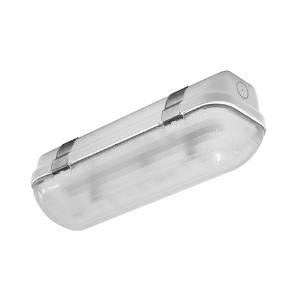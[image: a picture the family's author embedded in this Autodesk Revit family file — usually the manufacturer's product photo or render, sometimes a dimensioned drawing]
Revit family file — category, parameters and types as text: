
# Revit family: 3f_filippi_-_3f_linda_compatta_3f_filippi_-_5066_-_3f_linda_led_1x6w_l300
name_source: partatom
category: Lighting Fixtures
units: mm (PartAtom-declared; Revit-internal decimal feet)

## family parameters
Cut with Voids When Loaded = No
Host = Face
Light Source = No
Part Type = Normal
Room Calculation Point = No
Round Connector Dimension = Use Diameter
Shared = No

## types (1)
- 3F Filippi - 3F Linda Compatta (1 x LED, 883 lm, 7.5 W, 4000 K)
    Apparent Load = 8 VA
    Approval mark = ENEC
    CIE Flux Codes = 44 76 94 97 100
    Color Rendering = 80
    Color Temperature = 4000 K
    Control Gear = Electronic ballast
    Default Elevation = 1800 mm
    Description = ILLUMINOTECHNICAL
Luminous efficiency 100% (DLOR 97%, ULOR 3%).
Initial luminous flux of the luminaire 883 lm.
Controlled symmetric distribution.
Installation Interdistance Transv.D = 1.82 x hu - Long.D = 1.20 x hu.
Tabular UGR (CIE 117 - 4H-8H; S=0.25H; 70/50/20): RUG 21.6 - 22.5.
Beam angle: 110° - 66°.
Luminous efficacy 118 lm/W.
Lifetime (L93/B10): 30000 h. (tq+25°C)
Lifetime (L90/B10): 50000 h. (tq+25°C)
Lifetime (L85/B10): 80000 h. (tq+25°C)
Lifetime (L80/B10): 100000 h. (tq+25°C)
Sudden decreased luminous flux after 50000 hours: 0% (C0).
Photobiological safety in compliance with IEC/TR 62778: RG0 risk exempt, (IEC 62471).
In compliance with IEC/EN 62722-2-1 - IEC/EN 62717 standards.

SOURCE
Linear LED module 6W/840.
Energy efficiency class (UE 2019/2020 - UE 2019/2015): D.
CIE 13.3 Colour rendering index: CRI >80 (R9 <50%).
IES TM-30 Fidelity Index: Rf = 84 Rg = 95.
CCT nominal colour temperature 4000 K.
Colour initial tolerance (MacAdam): SDCM 3.

MECHANICAL
Self-extinguishing V2 polycarbonate housing, injection moulded, RAL 7035 grey.
Ecologic anti-aging injected sealing gasket.
Gear-holder reflector in hot-dip galvanised steel, painted with white polyester base.
Diffuser in self-extinguishing V2 polycarbonate, photo-engraved interior, UV stabilised, injection moulded with smooth outer surface.
Snug fit safety snap-lock clips for diffuser mounting in stainless steel, screwdriver opening.
Luminaire with limited surface temperature. - D - (EN 60598-2-24)
Dimensions: 300x100 mm, height 100 mm. Weight 0.555 kg.
IP66 protection degree.
Mechanical strength to impacts IK10 (20 joule).
Glow-wire test resistance 850°C.

ELECTRICAL
Halogen Free electronic wiring 230V-50/60Hz, power factor 0.88, THD <25%, constant output current, SELV, class I, 1 driver.
Power of the luminaire 7.5 W.
CE - IEC 60598-1 - EN 60598-1.
Flicker: <15%.
Luminaire compliant with EN 60598-2-22 for power supply from a centralised emergency system CPSS (Central Power Supply System), not incorporated in the luminaire - high risk areas excluded. The default power and flux are 100% in AC and 100% in DC.
Ambient temperature from -20°C to +35°C.
Temperature class T6 max 85°C.
Relative humidity UR: <85%.

INSTALLATION
Ceiling / Wall.
All accessories dedicated to this product are available on the Catalog and on our website www.3F-Filippi.com.

APPLICATIONS
Suitable product for food production plants (HACCP), IFS (Food Version 6), BRC (GSFS Food Version 7).
Dry, dusty indoor environments, subject to occasional water splashes.
Virtually shatterproof polycarbonate compatibly with the fumes / atmospheres that compromise the elasticity of plastic materials.
Not suitable for installation on surfaces subject to important vibrations, exposed to weather conditions, on ropes or poles.
Suitable for illumination of public car parks and parking grounds referred to DIN 67528:2018-04.

WARNING
Fixture not suitable for cold stores with an ambient temperature <0°C and/or relative humidity >85%.
Luminaire designed for disposal/recycling at end-of-life.
Replaceable (LED only) light source by a professional. Replaceable control gear by a professional.
    Height = 100 mm  [stored 0.328084 ft]
    Lamp = 1 x LED
    Lamp Light Flux = 883 lm
    Lamp Power = 7.5 W
    Lamp count = 1
    Length = 300 mm
    Lifetime = 50000 h
    Luminous efficacy = 118 lm/W
    Manufacturer = 3F Filippi
    ModVariant = No
    Model = 3F Filippi - 5066 - 3F Linda LED 1x6W L300
    Mounting Place = Ceiling
    Mounting Type = Pendant
    Number of Poles = 1
    OnlyDefault = Yes
    Power Factor = 1
    Product Name = 3F Filippi - 3F Linda Compatta
    Product group = pendant luminaire
    ProductGroupID = 9
    Protection Class = Protection class I
    Protection Degree = IP 66
    RLX_Detail_Level = 1
    RLX_Emergency_Light_Flux = 0 lm
    RLX_Emergency_Type = 0
    RLX_Emergency_Type_DB = No
    RlxData = <blob elided: 71909 chars, md5=bf844ade>
    Socket = socket
    Standby Power = 0 W
    System Light Flux = 883 lm
    System Power = 8 W
    Type Comments = Product without accessories
    Type Image = 3ffilippi_3f_linda_led_compatta_100.jpg
    URL = http://relux.com
    VarID = ---
    Voltage = 0 V
    Weight = 0.00 kg
    Width = 100 mm  [stored 0.328084 ft]

note: [stored X ft] marks values corroborated as IEEE doubles in the binary element streams (Revit-internal decimal feet)

## geometry (parser evidence)
native form markers: Blend x4, Sweep x8
no freeform markers — native parametric forms only
